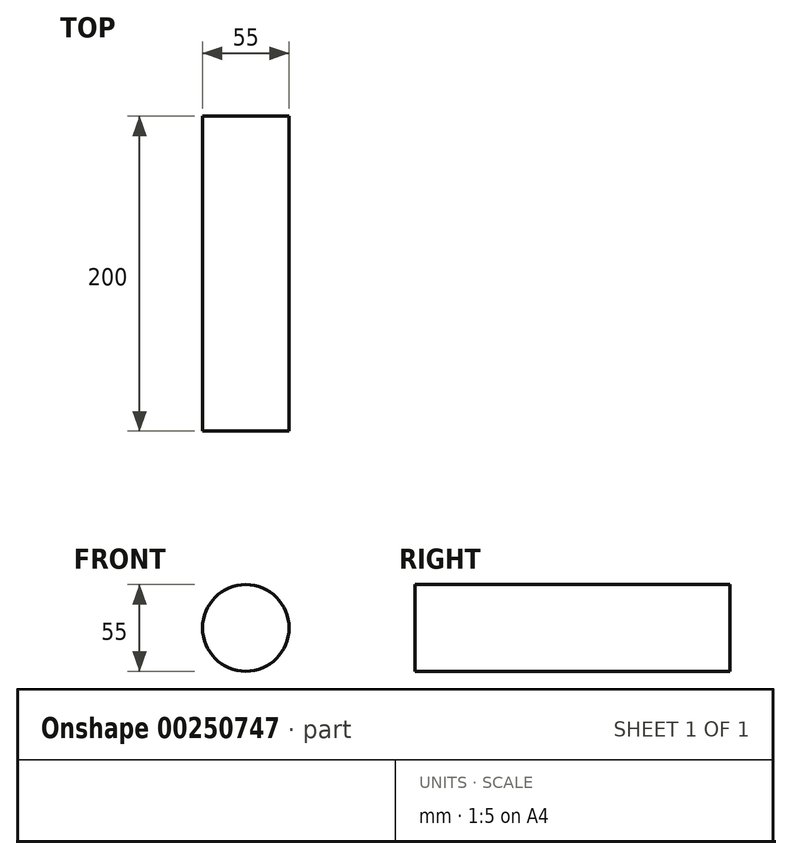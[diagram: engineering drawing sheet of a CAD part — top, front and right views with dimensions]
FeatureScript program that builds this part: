
annotation { "Feature Type Name" : "Feature", "Feature Type Description" : "" }
export const myFeature = defineFeature(function(context is Context, id is Id, definition is map)
    precondition{}
    {
        {
            var Q0;
            Q0=qCreatedBy(makeId("Front.planeOp"),FACE);
            var sketch = newSketch(context, id + "F0", { "sketchPlane" : qUnion([Q0])});
            skCircle(sketch, "E0", {"center": v(0, 0) * mm, "radius": 27.5 * mm});
            skSolve(sketch);
        }
        {
            var Q0;
            Q0=makeQuery(id+"F0.imprint","IMPRINT",FACE,{"disambiguationData":[TD([[makeQuery(id+"F0.imprint","IMPRINT",EDGE,{"derivedFrom":sQuery(id+"F0.wireOp",EDGE,"E0")}),1.0]])]});
            extrude(context, id + "F1", {"entities" : qUnion([Q0]), "depth" : 200 * mm});
        }
    });
